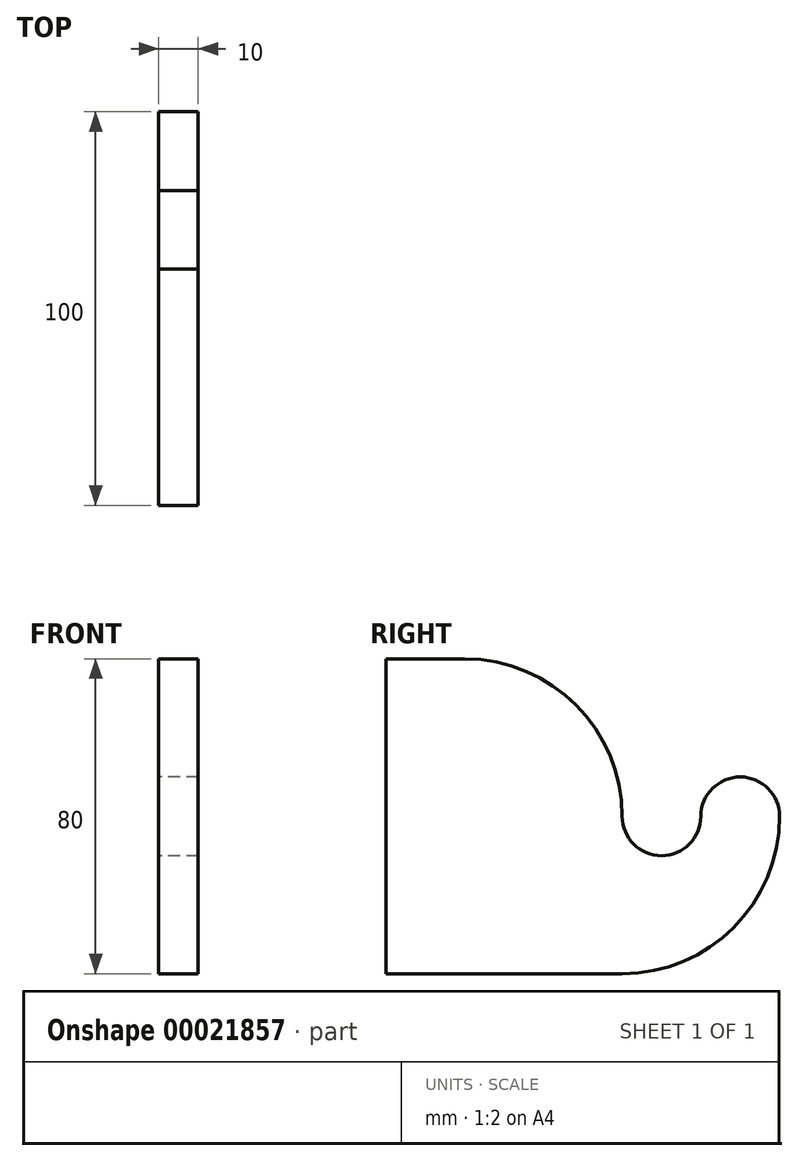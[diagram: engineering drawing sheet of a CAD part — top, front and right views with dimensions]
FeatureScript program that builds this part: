
annotation { "Feature Type Name" : "Feature", "Feature Type Description" : "" }
export const myFeature = defineFeature(function(context is Context, id is Id, definition is map)
    precondition{}
    {
        {
            var Q0;
            Q0=qCreatedBy(makeId("Right.planeOp"),FACE);
            var sketch = newSketch(context, id + "F0", { "sketchPlane" : qUnion([Q0])});
            skLineSegment(sketch, "E0.top", {"start": v(-60, -40) * mm, "end": v(0, -40) * mm});
            skLineSegment(sketch, "E0.left", {"start": v(-60, 40) * mm, "end": v(-60, -40) * mm});
            skArc(sketch, "E1", {"start": v(0, -40) * mm, "mid": v(28.28, -28.28) * mm, "end": v(40, 0) * mm});
            skArc(sketch, "E2", {"start": v(40, 0) * mm, "mid": v(30, 10) * mm, "end": v(20, 0) * mm});
            skArc(sketch, "E3", {"start": v(0, 0) * mm, "mid": v(10, -10) * mm, "end": v(20, 0) * mm});
            skPoint(sketch, "E4.center.orphan", {"position": v(-43.33, 0) * mm});
            skLineSegment(sketch, "E5", {"start": v(-40, 40) * mm, "end": v(-60, 40) * mm});
            skLineSegment(sketch, "E6", {"start": v(-40, 40) * mm, "end": v(-40, 40) * mm});
            skArc(sketch, "E7", {"start": v(-40, 40) * mm, "mid": v(-11.72, 28.28) * mm, "end": v(0, 0) * mm});
            skSolve(sketch);
        }
        {
            var Q0;
            Q0=makeQuery(id+"F0.imprint","IMPRINT",FACE,{"disambiguationData":[TD([[makeQuery(id+"F0.imprint","IMPRINT",EDGE,{"derivedFrom":sQuery(id+"F0.wireOp",EDGE,"E0.top")}),1.0]])]});
            extrude(context, id + "F1", {"entities" : qUnion([Q0]), "depth" : 10 * mm});
        }
    });
